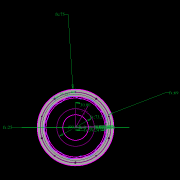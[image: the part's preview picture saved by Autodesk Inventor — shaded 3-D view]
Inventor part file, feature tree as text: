
AUTODESK INVENTOR PART (.ipt)
format: ipt  version: 2022.2 (Build 262287010, 287A)  size: 646,656 bytes
history: native  units: mm
features: extrude x28, other x19, sketch x17, pattern_circular x11, plane x4, fillet x2, move_body x2, revolve x2, draft x2, chamfer x2
ambient origin geometry x8: Origin, YZ Plane, XZ Plane, XY Plane, X Axis, Y Axis, Z Axis, Center Point
bodies: Solid5 (feature_tree)
feature tree (89):
  other  "CrossSection1"
  sketch  "Sketch7"  dims[d167=8.972256mm]
  other  "Roller1"
  other  "Roller2"
  sketch  "Sketch22"  dims[d173=10.814812mm]
  sketch  "Sketch2"  dims[d57=4.025mm d90=61.984365mm]
  sketch  "Sketch23"  dims[d201=75.0mm d232=0.0mm d233=3600.0mm]
  other  "RevRoller1"
  fillet  "Fillet1"  Radius=59.246882mm
  extrude  "Extrusion39"  Depth=61.984365mm
  pattern_circular  "Circular Pattern13"  Count=360  [1 undecoded]
  move_body  "Move Body7"
  revolve  "Revolution13"  [1 undecoded]
  fillet  "Fillet3"  Radius=0.025mm
  pattern_circular  "Circular Pattern14"  Count=24  [1 undecoded]
  move_body  "Move Body6"
  revolve  "Revolution14"  Angle=360.0deg
  other  "OuterRim_Top2"
  other  "OuterRim_Bottom2"
  plane  "Work Plane8"
  sketch  "Sketch49"  dims[d352=0.025mm]
  sketch  "Sketch50"  dims[d354=0.025mm]
  sketch  "Sketch51"  dims[d355=16.1595mm]
  extrude  "Extrusion40"  Depth=1.0mm
  extrude  "Extrusion41"  Depth=1.0mm
  extrude  "Extrusion42"  Depth=1.0mm
  extrude  "Extrusion43"  Depth=1.0mm
  sketch  "Sketch52"  dims[d356=16.159664mm]
  extrude  "Extrusion44"  Depth=1.0mm
  extrude  "Extrusion45"  TaperAngle=90.0deg  [1 undecoded]
  extrude  "Extrusion46"  Depth=1.0mm
  extrude  "Extrusion47"  Depth=1.0mm
  pattern_circular  "Circular Pattern32"  Angle=360.0deg  [1 undecoded]
  pattern_circular  "Circular Pattern33"  Angle=90.0deg  [1 undecoded]
  sketch  "Sketch57"  dims[d358=360.0deg]
  extrude  "Extrusion50"  Depth=0.1mm
  extrude  "Extrusion51"  Depth=1.0mm
  pattern_circular  "Circular Pattern34"  [2 undecoded]
  extrude  "Extrusion52"  Depth=1.0mm
  extrude  "Extrusion53"  Depth=1.0mm
  pattern_circular  "Circular Pattern35"  [2 undecoded]
  plane  "Work Plane7"
  sketch  "Sketch47"  dims[d350=47.575427mm]
  extrude  "Rotor_Ring"  TaperAngle=0.0deg  [1 undecoded]
  draft  "FaceDraft2"
  sketch  "Sketch30"  dims[d343=16.1595mm d344=16.159664mm d345=0.025mm]
  plane  "Work Plane5"
  other  "Rotor Featurs"
  other  "RotorRim_Bottom"
  extrude  "Extrusion24"  TaperAngle=0.0deg  [1 undecoded]
  extrude  "Extrusion25"  Depth=1.0mm
  extrude  "Extrusion26"  Depth=75.0mm
  pattern_circular  "Circular Pattern23"  [2 undecoded]
  sketch  "Sketch41"  dims[d347=0.1mm]
  extrude  "Extrusion27"  Depth=1.5mm
  extrude  "Extrusion28"  Depth=1.5mm
  pattern_circular  "Circular Pattern24"  [2 undecoded]
  extrude  "Extrusion29"  TaperAngle=90.0deg  [1 undecoded]
  extrude  "Extrusion30"  TaperAngle=90.0deg  [1 undecoded]
  extrude  "Extrusion31"  TaperAngle=90.0deg  [1 undecoded]
  pattern_circular  "Circular Pattern25"  [2 undecoded]
  sketch  "Sketch42"  dims[d348=0.1mm]
  extrude  "Extrusion32"  Depth=1.0mm
  extrude  "Extrusion33"  TaperAngle=0.0deg  [1 undecoded]
  extrude  "Extrusion34"  Depth=1.0mm
  extrude  "Extrusion35"  Depth=2.0mm TaperAngle=0.0deg
  pattern_circular  "Circular Pattern26"  [2 undecoded]
  pattern_circular  "Circular Pattern27"  [2 undecoded]
  chamfer  "Chamfer1"  Distance=13.856406mm
  chamfer  "Chamfer2"  Distance=2.5mm Angle=30.0deg
  draft  "FaceDraft4"
  plane  "Work Plane6"
  sketch  "Sketch43"  dims[d349=47.575591mm]
  extrude  "Extrusion37"  Depth=1.0mm
  extrude  "Extrusion38"  Depth=1.0mm TaperAngle=30.0deg
  other  "2D Equation Curve1"
  sketch  "Sketch40"  dims[d346=0.025mm]
  other  "Work Axis6"
  other  "Work Axis7"
  other  "Work Axis8"
  other  "Work Axis9"
  other  "Work Axis10"
  other  "Work Point1"
  other  "Work Point2"
  other  "Work Point3"
  other  "Work Point4"
  other  "Work Point5"
  sketch  "Sketch48"  dims[d351=0.025mm]
  sketch  "Sketch58"  dims[d359=0.5mm d360=240.0mm d361=360.0deg d363=1.308997mm d367=8.1mm d370=0.025mm d371=1.0mm d372=1.308997mm d373=90.0deg d374=0.5mm d375=240.0mm d376=360.0deg d378=90.0deg d379=0.1mm d380=0.025mm d381=0.025mm d382=0.025mm d383=0.025mm d384=11.193516mm d385=0.0mm d386=0.0mm d391=25.0mm d392=75.0mm d393=1.5mm d394=1.5mm d395=1.5mm d396=1.5mm d397=90.0deg d398=90.0deg d399=90.0deg d400=75.0mm d401=11.193516mm d402=0.0mm d486=0.436332mm d487=0.5mm d488=2.0mm d489=0.0mm d490=20.0mm d495=2.5mm d496=8.0mm d506=13.856406mm d507=55.5mm d508=8.0mm d509=0.05mm d510=2.5mm d511=30.0deg d512=12.0mm d513=6.0mm d514=0.2mm d515=30.0deg d516=131.0mm d517=65.5mm d518=0.2mm d519=100.0mm d520=120.0mm d521=2.0mm d522=150.0mm d530=50.0mm d531=5.5mm d532=5.5mm d533=5.5mm d534=85.75mm d535=73.5mm d536=61.25mm d537=24.5mm d538=3.0mm d539=2.4mm d540=0.0mm d541=0.0mm d542=0.0mm d543=5.5mm d544=3.0mm d545=0.0mm d546=90.0mm d547=360.0deg d549=3.0mm d550=3.0mm d551=2.4mm d552=0.0mm d553=5.596758mm d554=0.0mm d555=2.4mm d556=0.0mm d557=5.596758mm d558=0.0mm d559=5.596758mm d560=0.0mm d561=90.0mm d562=360.0deg d564=60.0mm d565=360.0deg d567=5.5mm d568=5.5mm d569=3.0mm d570=0.0mm d571=5.596758mm d572=0.0mm d573=3.0mm d574=0.0mm d575=5.596758mm d576=0.0mm d577=90.0mm d578=360.0deg d580=60.0mm d581=360.0deg d584=20.0mm d585=8.0mm d587=1.75mm d589=3.0mm d592=2.0mm d593=12.0mm d594=12.0mm d600=0.5mm d601=2.0mm d602=45.0deg d603=0.5mm d604=2.0mm d605=45.0deg d606=0.436332mm d607=0.5mm d608=0.0mm d609=20.0mm d611=360.0deg d613=0.0mm d614=0.0mm d617=0.99971mm d618=100.0mm d620=69.0mm d621=5.0mm d622=0.5mm d623=0.5mm d624=5.0mm d625=0.2mm d626=0.0mm d627=20.0mm d629=69.0mm d630=73.5mm d631=20.0mm d633=6.283185mm d635=5.5mm d636=3.0mm d637=7.0mm d638=4.0mm d639=5.596758mm d640=0.0mm d641=3.0mm d642=0.0mm d643=5.596758mm d644=0.0mm d645=4.0mm d646=0.0mm d647=20.0mm d649=6.283185mm d651=3.0mm d652=4.0mm d653=20.0mm d655=6.283185mm d657=7.0mm d658=5.5mm d659=5.596758mm d660=0.0mm d661=2.593516mm d662=0.0mm d663=5.596758mm d664=0.0mm d665=3.193516mm d666=0.0mm d679=50.0mm d680=360.0deg d682=50.0mm d683=360.0deg d694=6.35mm d695=6.35mm d696=6.2mm d697=6.2mm d698=11.194mm d699=0.0mm d700=8.194mm d701=0.0mm d702=60.0mm d703=360.0deg d705=30.0deg d706=4.0mm d707=7.0mm d708=3.193516mm d709=0.0mm d710=11.193516mm d711=0.0mm d712=60.0mm d713=360.0deg d16=0.872665mm d17=0.872665mm d49=0.872665mm d50=0.872665mm d51=0.872665mm d52=0.872665mm d236=0.5mm d237=0.872665mm d238=0.5mm d239=0.872665mm d282=1.0mm d283=1.0mm d284=1.0mm d285=0.15mm d286=0.25mm d287=0.375mm d288=14.3117mm d289=0.75mm d290=20.594885mm d291=0.0625mm d292=0.75mm d293=0.375mm d405=0.5mm d406=0.872665mm d407=0.5mm d408=0.872665mm d413=0.5mm d414=0.872665mm d415=0.5mm d416=0.872665mm d417=0.5mm d418=0.872665mm d419=0.5mm d420=0.872665mm d421=0.872665mm d431=0.5mm d432=0.872665mm d433=0.5mm d434=0.872665mm d471=0.5mm d472=0.872665mm d473=0.5mm d474=0.872665mm d497=0.5mm d498=0.872665mm d499=0.5mm d500=0.872665mm d590=0.5mm d591=0.872665mm]
note: 26 required parameter values undecoded (feature->parameter linkage not recoverable at this tier; creation-order binding heuristic only, values carry confidence <= 0.55)